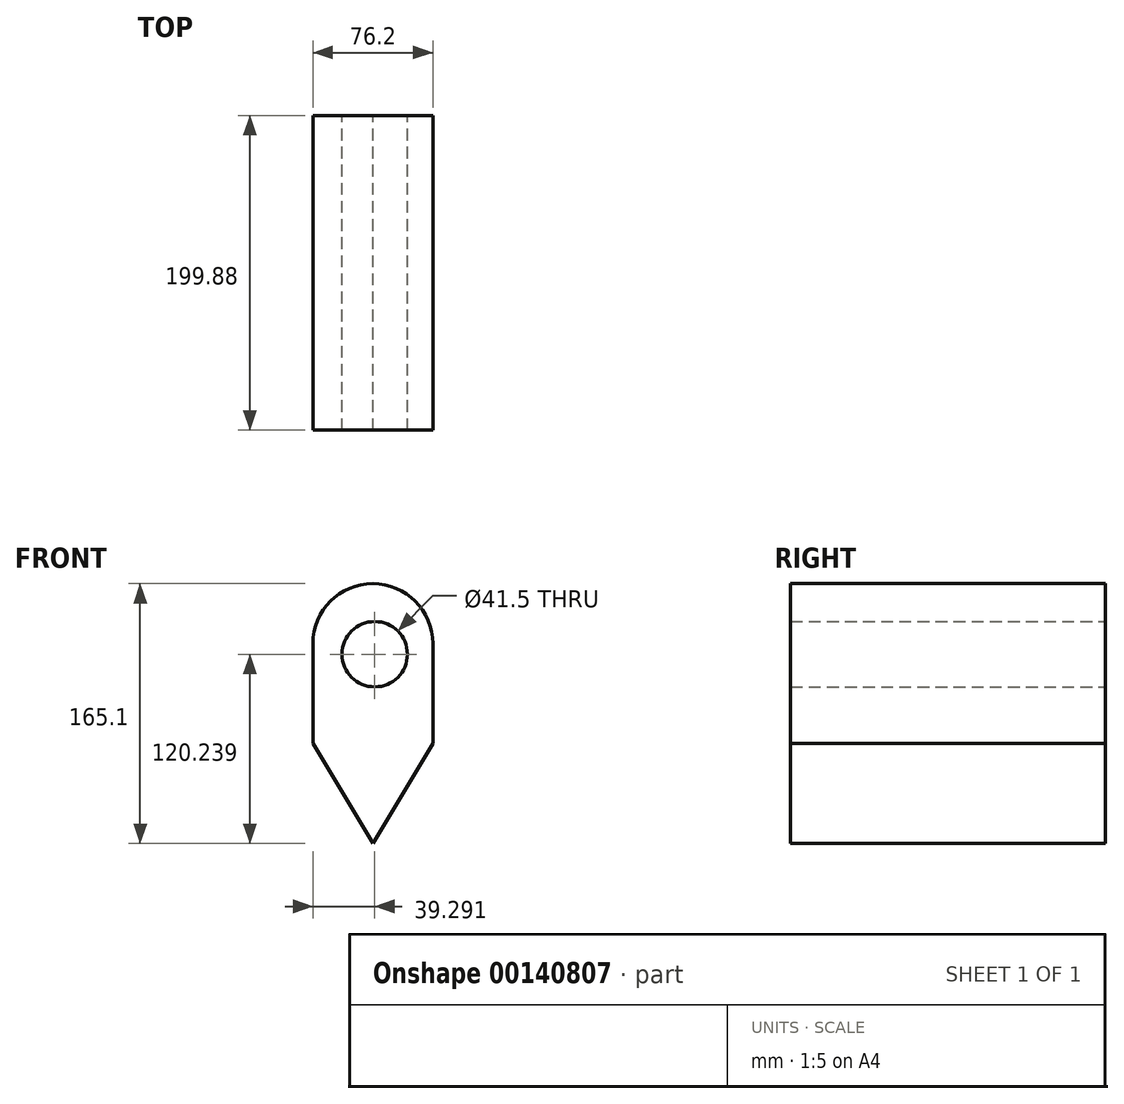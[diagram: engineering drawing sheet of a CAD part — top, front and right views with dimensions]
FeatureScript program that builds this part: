
annotation { "Feature Type Name" : "Feature", "Feature Type Description" : "" }
export const myFeature = defineFeature(function(context is Context, id is Id, definition is map)
    precondition{}
    {
        {
            var Q0;
            Q0=qCreatedBy(makeId("Front.planeOp"),FACE);
            var sketch = newSketch(context, id + "F0", { "sketchPlane" : qUnion([Q0])});
            skLineSegment(sketch, "E0.bottom", {"start": v(0, 0) * mm, "end": v(76.2, 0) * mm});
            skLineSegment(sketch, "E0.top", {"start": v(0, 127) * mm, "end": v(76.2, 127) * mm});
            skLineSegment(sketch, "E0.left", {"start": v(0, 0) * mm, "end": v(0, 127) * mm});
            skLineSegment(sketch, "E0.right", {"start": v(76.2, 0) * mm, "end": v(76.2, 127) * mm});
            skCircle(sketch, "E1", {"center": v(38.1, 127) * mm, "radius": 38.1 * mm});
            skLineSegment(sketch, "E2", {"start": v(0, 63.5) * mm, "end": v(38.1, 0) * mm});
            skLineSegment(sketch, "E3", {"start": v(38.1, 0) * mm, "end": v(76.2, 63.5) * mm});
            skSolve(sketch);
        }
        {
            var Q0;
            {var subQ0=sQuery(id+"F0.wireOp",EDGE,"E2");Q0=makeQuery(id+"F0.imprint","IMPRINT",FACE,{"disambiguationData":[TD([[makeQuery(id+"F0.imprint","IMPRINT",EDGE,{"derivedFrom":subQ0}),1.0]])]});}
            var Q1;
            {var subQ0=sQuery(id+"F0.wireOp",EDGE,"E0.top");Q1=makeQuery(id+"F0.imprint","IMPRINT",FACE,{"disambiguationData":[TD([[makeQuery(id+"F0.imprint","IMPRINT",EDGE,{"derivedFrom":subQ0}),-1.0]])]});}
            var Q2;
            {var subQ0=sQuery(id+"F0.wireOp",EDGE,"E0.top");Q2=makeQuery(id+"F0.imprint","IMPRINT",FACE,{"disambiguationData":[TD([[makeQuery(id+"F0.imprint","IMPRINT",EDGE,{"derivedFrom":subQ0}),1.0]])]});}
            extrude(context, id + "F1", {"entities" : qUnion([Q0, Q1, Q2]), "depth" : 199.88 * mm});
        }
        {
            var Q0;
            Q0=makeQuery(id+"F1.opExtrude","CAP_FACE",FACE,{"disambiguationData":[OSD([sQuery(id+"F0.wireOp",EDGE,"E0.left"),sQuery(id+"F0.wireOp",EDGE,"E0.right"),sQuery(id+"F0.wireOp",EDGE,"E1"),sQuery(id+"F0.wireOp",EDGE,"E2"),sQuery(id+"F0.wireOp",EDGE,"E3")])],"isStart":true});
            var sketch = newSketch(context, id + "F2", { "sketchPlane" : qUnion([Q0])});
            skCircle(sketch, "E4", {"center": v(-39.3, 120.24) * mm, "radius": 20.75 * mm});
            skSolve(sketch);
        }
        {
            var Q0;
            Q0 = qSketchRegion(id + "F2", true);
            extrude(context, id + "F3", {"entities" : qUnion([Q0]), "operationType" : NewBodyOperationType.REMOVE, "oppositeDirection" : true, "depth" : 239.78 * mm});
        }
    });
